# Revit family: ABR-BWS2-1548xWS840T1600
name_source: partatom
category: Leuchten
units: mm (PartAtom-declared; Revit-internal decimal feet)

## family parameters
Basisbauteil = Fläche
Beim Laden mit Abzugskörper schneiden = Nein
Bemaßung runder Anschluss = Durchmesser verwenden
Gemeinsam genutzt = Nein
Lichtquelle = Ja
OmniClass-Nummer = 23.80.70.11
OmniClass-Titel = Luminaries for Internal Lighting
Raumberechnungspunkt = Nein
Teiletyp = Normal

## types (2) — shared parameters
Baugruppenkennzeichen = D5020200
Datei für fotometrisches Netz = ABR_EBR-BWS_2-3-4.IES
Emissionsform beim Rendern sichtbar = Nein
Farbfilter = 16777215
Farbtemperaturverschiebung bei Dämpfen der Lampe = <Keine Auswahl>
Hersteller = RIDI Leuchten GmbH
Lampe = LED
Neigungswinkel = 90.00°
Scheinlast = 106 VA
URL = www.ridi.de
Von Breite des Rechtecks ausssenden = 1520 mm
Von Länge des Rechtecks aussenden = 264 mm  [stored 0.866142 ft]
brand = RIDI
conformity mark = CE
electrical safety class = 1
height = 90 mm  [stored 0.295276 ft]
ingress protection (IP) code = IP20
length = 1549 mm  [stored 5.08202 ft]
nominal frequency = 50-60Hz
nominal voltage = 230
rated input power = 106
voltage type (AC, DC, UC) = AC
weight = 10,3 kg
width = 314 mm  [stored 1.03018 ft]
zero-valued in all types: Vorgabe-Ansicht

## per-type parameters (varying)
| type | Modell |
| ABR-BWS2 1549FLWS840T1400 | 0650984 |
| ABR-BWS2 1549DAWS840T1400 | 0660984 |

note: column(s) folded — value = type name in every type: product name

note: [stored X ft] marks values corroborated as IEEE doubles in the binary element streams (Revit-internal decimal feet)
